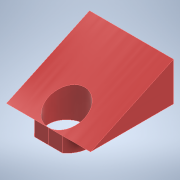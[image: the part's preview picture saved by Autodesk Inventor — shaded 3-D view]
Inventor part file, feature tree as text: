
AUTODESK INVENTOR PART (.ipt)
format: ipt  version: 2022.2 (Build 262287000, 287)  size: 154,624 bytes
history: native  units: mm
features: extrude x3, sketch x2
ambient origin geometry x8: Origin, YZ Plane, XZ Plane, XY Plane, X Axis, Y Axis, Z Axis, Center Point
bodies: Solid6 (feature_tree)
feature tree (5):
  extrude  "Extrusion34"  Depth=139.7mm TaperAngle=0.0deg
  sketch  "Sketch67"  dims[d338=60.325mm d339=8.0mm d344=8.0mm d345=0.0mm d346=0.0mm d347=25.0mm d348=0.0mm d349=152.4mm d64=1.0mm d65=1.0mm d66=1.0mm d67=0.15mm d68=0.25mm d69=0.375mm d70=14.3117mm d71=0.75mm d72=20.594885mm d73=0.0625mm d74=0.75mm d75=0.375mm]
  extrude  "Extrusion37"  Depth=152.4mm
  extrude  "Extrusion38"  Depth=152.4mm
  sketch  "Sketch65"  dims[d335=4.363323mm d336=139.7mm d337=0.0mm]
